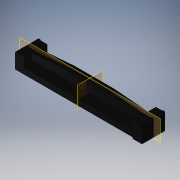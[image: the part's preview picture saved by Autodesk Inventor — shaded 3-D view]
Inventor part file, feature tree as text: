
AUTODESK INVENTOR PART (.ipt)
format: ipt  version: 2019 (Build 230136000, 136)  size: 229,376 bytes
history: native  units: mm (DEFAULTED — no unit token found)
features: other x16, sketch x8, extrude x5, fillet x1, pattern_linear x1
ambient origin geometry x8: Origin, YZ Plane, XZ Plane, XY Plane, X Axis, Y Axis, Z Axis, Center Point
bodies: Solid1 (feature_tree)
feature tree (31):
  extrude  "Extrusion1"  Depth=10.0mm
  extrude  "Extrusion2"  Depth=47.0mm
  extrude  "Extrusion3"  Depth=7.4676mm TaperAngle=0.0deg
  extrude  "Extrusion4"  Depth=2.54mm
  extrude  "Extrusion5"  Depth=1.3208mm
  fillet  "Fillet1"  Radius=0.762mm
  sketch  "Sketch8"  dims[d15=8.128mm]
  sketch  "Sketch9"  dims[d16=16.891mm]
  sketch  "Sketch11"  dims[d17=0.508mm d18=3.302mm d19=0.0mm d20=1.143mm d21=3.302mm d22=0.0mm d23=0.5842mm d37=0.508mm d38=0.5842mm d39=0.254mm d40=160.0mm d42=1.27mm d43=10.0mm d45=25.4mm d48=1.27mm d49=1.27mm d50=1.27mm d51=1.27mm d53=1.27mm d54=1.27mm d55=1.27mm d56=1.27mm d57=1.27mm d58=1.27mm d59=1.27mm d60=1.27mm d61=1.27mm d62=1.27mm d63=1.27mm d64=0.4318mm d65=2.032mm d66=20.0mm d68=22.86mm]
  pattern_linear  "Rectangular Pattern1"  Spacing1=3.302mm  [1 undecoded]
  sketch  "Sketch1"  dims[d0=55.0mm d1=10.0mm]
  sketch  "Sketch2"  dims[d2=7.4676mm d3=0.0mm d4=47.0mm]
  sketch  "Sketch3"  dims[d5=0.5842mm d6=7.4676mm d7=0.0mm]
  sketch  "Sketch4"  dims[d8=47.0mm d9=2.54mm]
  sketch  "Sketch5"  dims[d11=7.4676mm d12=0.0mm d13=1.3208mm d14=0.762mm]
  other  "Work Point66"
  other  "Work Point67"
  other  "Work Point68"
  other  "Work Point69"
  other  "Work Point70"
  other  "Work Point71"
  other  "Work Point72"
  other  "Work Point73"
  other  "Work Point74"
  other  "Work Point75"
  other  "Work Point76"
  other  "Work Point77"
  other  "Work Point78"
  other  "Work Point79"
  other  "Work Point80"
  other  "Work Point81"
note: 1 required parameter value undecoded (feature->parameter linkage not recoverable at this tier; creation-order binding heuristic only, values carry confidence <= 0.55)
